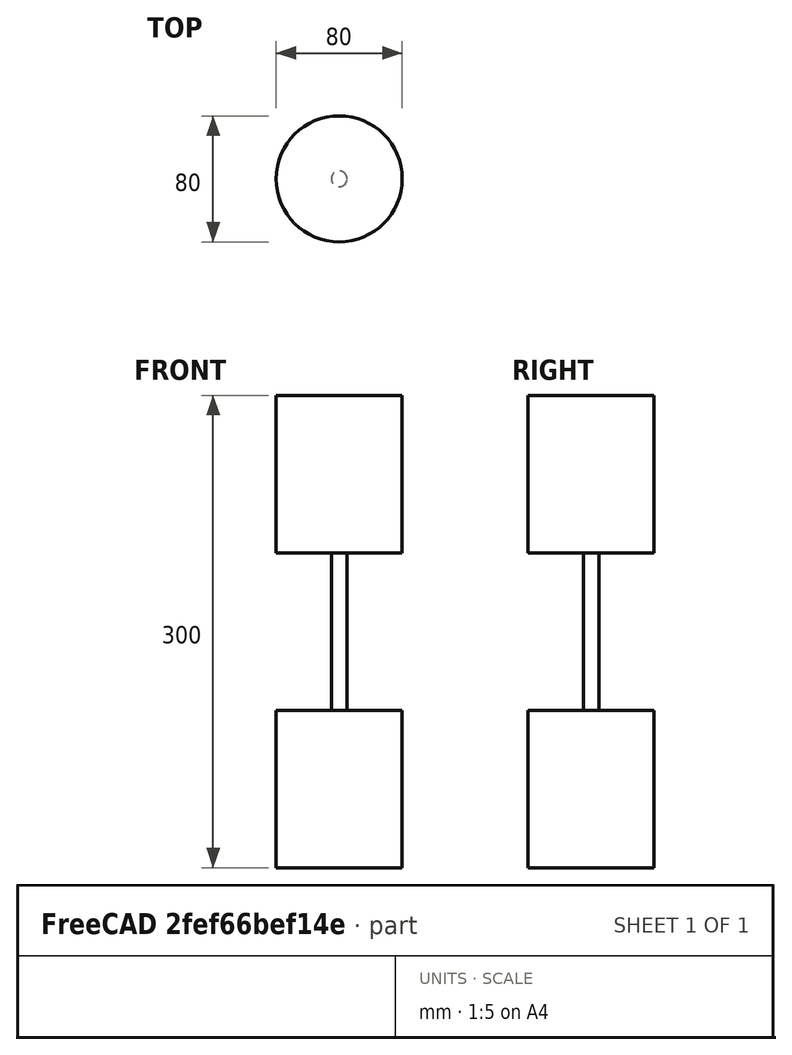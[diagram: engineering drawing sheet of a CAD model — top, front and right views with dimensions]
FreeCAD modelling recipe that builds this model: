
FCSTD DOCUMENT  (FreeCAD 0.20R29177 (Git))
Label: model
License: All rights reserved
LicenseURL: http://en.wikipedia.org/wiki/All_rights_reserved
objects: Part::Feature×7, Part::Cylinder×3, Part::Fuse×1
note: 11 computed .brp shape members not serialized (recipe doc carries the construction recipe); baked Part::Feature solids carry a one-line shape summary decoded from their .brp

FEATURE [Part::Cylinder] Cylinder  label="円柱"
  Angle = 360
  AttacherType = Attacher::AttachEngine3D
  FirstAngle = 0
  Height = 100
  Radius = 40
  SecondAngle = 0
FEATURE [Part::Cylinder] Cylinder001  label="円柱001"
  Angle = 360
  AttacherType = Attacher::AttachEngine3D
  FirstAngle = 0
  Height = 100
  Placement = pos=(0,0,100) rot=(0,0,1;0rad)
  Radius = 5
  SecondAngle = 0
FEATURE [Part::Cylinder] Cylinder002  label="円柱002"
  Angle = 360
  AttacherType = Attacher::AttachEngine3D
  FirstAngle = 0
  Height = 100
  Placement = pos=(0,0,200) rot=(0,0,1;0rad)
  Radius = 40
  SecondAngle = 0
FEATURE [Part::Fuse] Fusion
  Base = -> Cylinder
  Tool = -> Cylinder001
FEATURE [Part::Feature] Face006  label="zmin"
  shape: bbox 80 x 80 x 2e-07 mm, 1 faces, 0 solids (baked)
FEATURE [Part::Feature] Face002  label="zmax"
  Placement = pos=(0,0,300) rot=(0,0,1;0rad)
  shape: bbox 80 x 80 x 2e-07 mm, 1 faces, 0 solids (baked)
FEATURE [Part::Feature] Face  label="wall1"
  shape: bbox 80 x 80 x 100 mm, 1 faces, 0 solids (baked)
FEATURE [Part::Feature] Face007  label="wall2"
  shape: bbox 80 x 80 x 2e-07 mm, 1 faces, 0 solids (baked)
FEATURE [Part::Feature] Face008  label="wall3"
  Placement = pos=(0,0,200) rot=(0,0,1;0rad)
  shape: bbox 80 x 80 x 100 mm, 1 faces, 0 solids (baked)
FEATURE [Part::Feature] Face009  label="wall4"
  shape: bbox 80 x 80 x 2e-07 mm, 1 faces, 0 solids (baked)
FEATURE [Part::Feature] Face010  label="thin_wall"
  Placement = pos=(0,0,100) rot=(0,0,1;0rad)
  shape: bbox 10 x 10 x 100 mm, 1 faces, 0 solids (baked)
